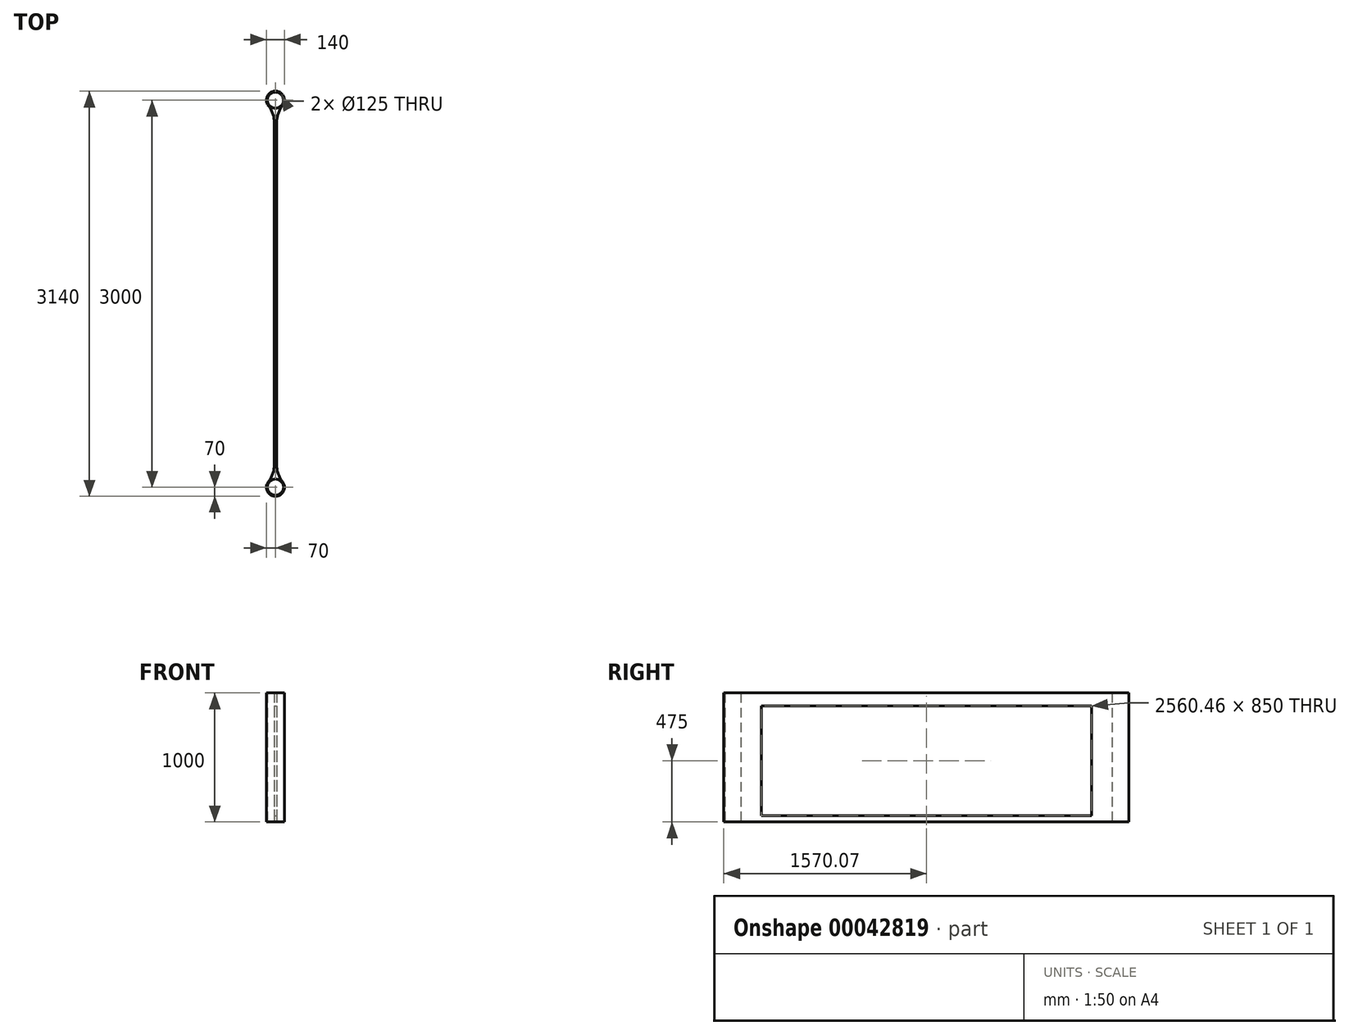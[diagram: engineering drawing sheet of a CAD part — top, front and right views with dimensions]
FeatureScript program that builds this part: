
annotation { "Feature Type Name" : "Feature", "Feature Type Description" : "" }
export const myFeature = defineFeature(function(context is Context, id is Id, definition is map)
    precondition{}
    {
        {
            var Q0;
            Q0=qCreatedBy(makeId("Top.planeOp"),FACE);
            var sketch = newSketch(context, id + "F0", { "sketchPlane" : qUnion([Q0])});
            skCircle(sketch, "E0", {"center": v(0, -1500) * mm, "radius": 62.5 * mm});
            skLineSegment(sketch, "E1", {"start": v(0, -1500) * mm, "end": v(0, 0) * mm, "construction": true});
            skLineSegment(sketch, "E2", {"start": v(0, 0) * mm, "end": v(0, 1500) * mm, "construction": true});
            skCircle(sketch, "E3", {"center": v(0, 1500) * mm, "radius": 62.5 * mm});
            skCircle(sketch, "E4", {"center": v(0, 1500) * mm, "radius": 70 * mm});
            skCircle(sketch, "E5", {"center": v(0, -1500) * mm, "radius": 70 * mm});
            skLineSegment(sketch, "E6.left", {"start": v(0, 1430) * mm, "end": v(-0.1, -1430) * mm});
            skLineSegment(sketch, "E6.right", {"start": v(10, 1430.72) * mm, "end": v(9.9, -1430.7) * mm});
            skLineSegment(sketch, "E7.left", {"start": v(0, 1430) * mm, "end": v(0.08, -1430) * mm});
            skLineSegment(sketch, "E7.right", {"start": v(-9.43, 1430.64) * mm, "end": v(-9.34, -1430.63) * mm});
            skSolve(sketch);
        }
        {
            var Q0;
            {var subQ1=sQuery(id+"F0.wireOp",EDGE,"E7.left");Q0=makeQuery(id+"F0.imprint","IMPRINT",FACE,{"disambiguationData":[TD([[makeQuery(id+"F0.imprint","IMPRINT",EDGE,{"derivedFrom":subQ1}),-1.0]])]});}
            var Q1;
            {var subQ1=sQuery(id+"F0.wireOp",EDGE,"E6.right");Q1=makeQuery(id+"F0.imprint","IMPRINT",FACE,{"disambiguationData":[TD([[makeQuery(id+"F0.imprint","IMPRINT",EDGE,{"derivedFrom":subQ1}),-1.0]])]});}
            var Q2;
            Q2=makeQuery(id+"F0.imprint","IMPRINT",FACE,{"disambiguationData":[TD([[makeQuery(id+"F0.imprint","IMPRINT",EDGE,{"derivedFrom":sQuery(id+"F0.wireOp",EDGE,"E3")}),-1.0]])]});
            var Q3;
            Q3=makeQuery(id+"F0.imprint","IMPRINT",FACE,{"disambiguationData":[TD([[makeQuery(id+"F0.imprint","IMPRINT",EDGE,{"derivedFrom":sQuery(id+"F0.wireOp",EDGE,"E0")}),-1.0]])]});
            extrude(context, id + "F1", {"entities" : qUnion([Q0, Q1, Q2, Q3]), "depth" : 1000 * mm});
        }
        {
            var Q0;
            Q0=makeQuery(id+"F1.opExtrude","SWEPT_EDGE",EDGE,{"disambiguationData":[OSD([sQuery(id+"F0.wireOp",EDGE,"E5"),sQuery(id+"F0.wireOp",EDGE,"E7.right")])]});
            var Q1;
            Q1=makeQuery(id+"F1.opExtrude","SWEPT_EDGE",EDGE,{"disambiguationData":[OSD([sQuery(id+"F0.wireOp",EDGE,"E5"),sQuery(id+"F0.wireOp",EDGE,"E6.right")])]});
            var Q2;
            Q2=makeQuery(id+"F1.opExtrude","SWEPT_EDGE",EDGE,{"disambiguationData":[OSD([sQuery(id+"F0.wireOp",EDGE,"E4"),sQuery(id+"F0.wireOp",EDGE,"E6.right")])]});
            var Q3;
            Q3=makeQuery(id+"F1.opExtrude","SWEPT_EDGE",EDGE,{"disambiguationData":[OSD([sQuery(id+"F0.wireOp",EDGE,"E4"),sQuery(id+"F0.wireOp",EDGE,"E7.right")])]});
            fillet(context, id + "F2", {"entities" : qUnion([Q0, Q1, Q2, Q3]), "radius" : 200 * mm, "tangentPropagation" : true, "allowEdgeOverflow" : false});
        }
        {
            var Q0;
            Q0=makeQuery(id+"F1.opExtrude","SWEPT_FACE",FACE,{"disambiguationData":[OSD([sQuery(id+"F0.wireOp",EDGE,"E6.right")])]});
            var sketch = newSketch(context, id + "F3", { "sketchPlane" : qUnion([Q0])});
            skLineSegment(sketch, "E8", {"start": v(-1280.17, 1000) * mm, "end": v(-1280.17, 0) * mm});
            skLineSegment(sketch, "E9", {"start": v(1280.3, 1000) * mm, "end": v(1280.3, 0) * mm});
            skLineSegment(sketch, "E10", {"start": v(-1280.17, 900) * mm, "end": v(1280.3, 900) * mm});
            skLineSegment(sketch, "E11", {"start": v(-1280.17, 50) * mm, "end": v(1280.3, 50) * mm});
            skSolve(sketch);
        }
        {
            var Q0;
            {var subQ1=sQuery(id+"F3.wireOp",EDGE,"E10");Q0=makeQuery(id+"F3.imprint","IMPRINT",FACE,{"disambiguationData":[TD([[makeQuery(id+"F3.imprint","IMPRINT",EDGE,{"derivedFrom":subQ1}),-1.0]])]});}
            extrude(context, id + "F4", {"entities" : qUnion([Q0]), "operationType" : NewBodyOperationType.REMOVE, "endBound" : BoundingType.THROUGH_ALL, "oppositeDirection" : true, "depth" : 25 * mm});
        }
    });
